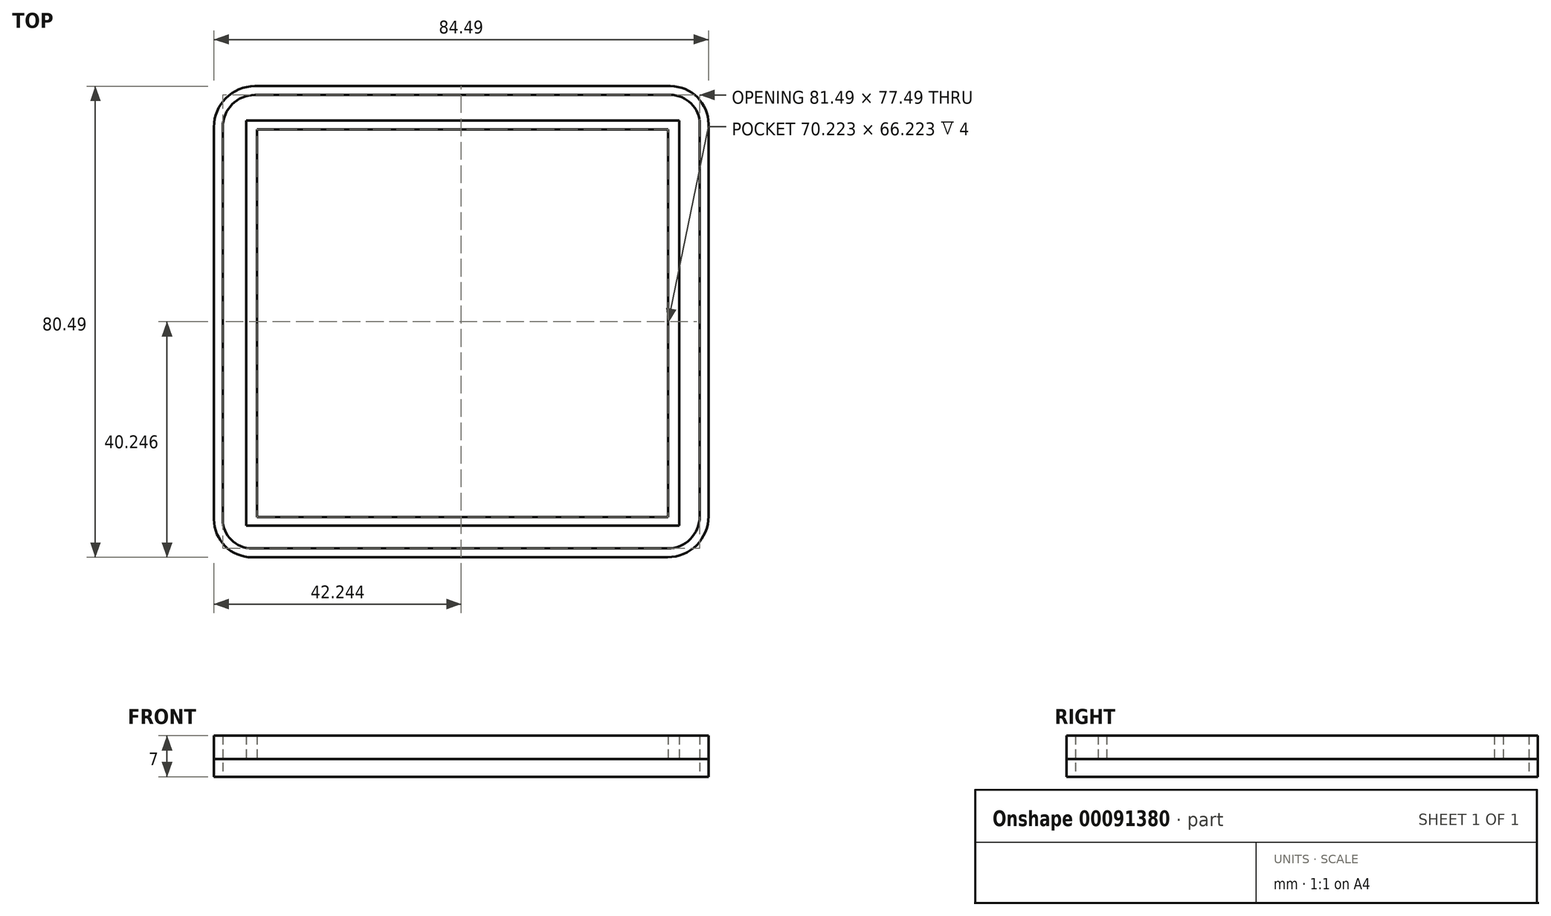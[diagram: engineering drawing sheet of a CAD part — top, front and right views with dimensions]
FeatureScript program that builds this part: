
annotation { "Feature Type Name" : "Feature", "Feature Type Description" : "" }
export const myFeature = defineFeature(function(context is Context, id is Id, definition is map)
    precondition{}
    {
        {
            var Q0;
            Q0=qCreatedBy(makeId("Top.planeOp"),FACE);
            var sketch = newSketch(context, id + "F0", { "sketchPlane" : qUnion([Q0])});
            skArc(sketch, "E0.0", {"start": v(-35.5, 39) * mm, "mid": v(-39.38, 37.38) * mm, "end": v(-41, 33.5) * mm});
            skLineSegment(sketch, "E0.1", {"start": v(-35.5, 39) * mm, "end": v(35.5, 39) * mm});
            skLineSegment(sketch, "E0.2", {"start": v(-37, 34.61) * mm, "end": v(37, 34.61) * mm});
            skLineSegment(sketch, "E0.4", {"start": v(-37, -34.61) * mm, "end": v(37, -34.61) * mm});
            skArc(sketch, "E0.6", {"start": v(40.5, 34) * mm, "mid": v(39.04, 37.53) * mm, "end": v(35.5, 39) * mm});
            skLineSegment(sketch, "E0.7", {"start": v(40.5, 34) * mm, "end": v(40.5, -33) * mm});
            skArc(sketch, "E0.8", {"start": v(35, -38.5) * mm, "mid": v(38.9, -36.9) * mm, "end": v(40.5, -33) * mm});
            skLineSegment(sketch, "E0.9", {"start": v(-36, -38.5) * mm, "end": v(35, -38.5) * mm});
            skLineSegment(sketch, "E0.10", {"start": v(-41, 33.5) * mm, "end": v(-41, -33.5) * mm});
            skArc(sketch, "E0.11", {"start": v(-41, -33.5) * mm, "mid": v(-39.53, -37.04) * mm, "end": v(-36, -38.5) * mm});
            skLineSegment(sketch, "E1.0", {"start": v(42, 34) * mm, "end": v(42, -33) * mm});
            skArc(sketch, "E1.1", {"start": v(35, -40) * mm, "mid": v(39.95, -37.95) * mm, "end": v(42, -33) * mm});
            skArc(sketch, "E1.2", {"start": v(42, 34) * mm, "mid": v(40.1, 38.59) * mm, "end": v(35.5, 40.5) * mm});
            skLineSegment(sketch, "E1.3", {"start": v(-36, -40) * mm, "end": v(35, -40) * mm});
            skLineSegment(sketch, "E1.4", {"start": v(-35.5, 40.5) * mm, "end": v(35.5, 40.5) * mm});
            skArc(sketch, "E1.5", {"start": v(-35.5, 40.5) * mm, "mid": v(-40.44, 38.44) * mm, "end": v(-42.5, 33.5) * mm});
            skLineSegment(sketch, "E1.6", {"start": v(-42.5, 33.5) * mm, "end": v(-42.5, -33.5) * mm});
            skArc(sketch, "E1.7", {"start": v(-42.5, -33.5) * mm, "mid": v(-40.59, -38.1) * mm, "end": v(-36, -40) * mm});
            skLineSegment(sketch, "E2.0", {"start": v(35.11, 33.11) * mm, "end": v(35.11, -33.11) * mm});
            skLineSegment(sketch, "E2.1", {"start": v(-35.11, 33.11) * mm, "end": v(35.11, 33.11) * mm});
            skLineSegment(sketch, "E2.2", {"start": v(-35.11, 33.11) * mm, "end": v(-35.11, -33.11) * mm});
            skLineSegment(sketch, "E2.3", {"start": v(-35.11, -33.11) * mm, "end": v(35.11, -33.11) * mm});
            skLineSegment(sketch, "E3", {"start": v(37, -34.61) * mm, "end": v(37, 34.61) * mm});
            skLineSegment(sketch, "E4", {"start": v(-37, 34.61) * mm, "end": v(-37, -34.61) * mm});
            skSolve(sketch);
        }
        {
            var Q0;
            Q0=makeQuery(id+"F0.imprint","IMPRINT",FACE,{"disambiguationData":[TD([[makeQuery(id+"F0.imprint","IMPRINT",EDGE,{"derivedFrom":sQuery(id+"F0.wireOp",EDGE,"E2.0")}),-1.0]])]});
            var Q1;
            Q1=makeQuery(id+"F0.imprint","IMPRINT",FACE,{"disambiguationData":[TD([[makeQuery(id+"F0.imprint","IMPRINT",EDGE,{"derivedFrom":sQuery(id+"F0.wireOp",EDGE,"E0.2")}),-1.0]])]});
            var Q2;
            Q2=makeQuery(id+"F0.imprint","IMPRINT",FACE,{"disambiguationData":[TD([[makeQuery(id+"F0.imprint","IMPRINT",EDGE,{"derivedFrom":sQuery(id+"F0.wireOp",EDGE,"E0.0")}),1.0]])]});
            var Q3;
            Q3=makeQuery(id+"F0.imprint","IMPRINT",FACE,{"disambiguationData":[TD([[makeQuery(id+"F0.imprint","IMPRINT",EDGE,{"derivedFrom":sQuery(id+"F0.wireOp",EDGE,"E0.0")}),-1.0]])]});
            extrude(context, id + "F1", {"entities" : qUnion([Q0, Q1, Q2, Q3]), "depth" : 3 * mm});
        }
        {
            var Q0;
            Q0=makeQuery(id+"F0.imprint","IMPRINT",FACE,{"disambiguationData":[TD([[makeQuery(id+"F0.imprint","IMPRINT",EDGE,{"derivedFrom":sQuery(id+"F0.wireOp",EDGE,"E0.0")}),-1.0]])]});
            extrude(context, id + "F2", {"entities" : qUnion([Q0]), "depth" : 7 * mm});
        }
        {
            var Q0;
            Q0=makeQuery(id+"F0.imprint","IMPRINT",FACE,{"disambiguationData":[TD([[makeQuery(id+"F0.imprint","IMPRINT",EDGE,{"derivedFrom":sQuery(id+"F0.wireOp",EDGE,"E0.2")}),-1.0]])]});
            extrude(context, id + "F3", {"entities" : qUnion([Q0]), "operationType" : NewBodyOperationType.ADD, "depth" : 7 * mm});
        }
    });
